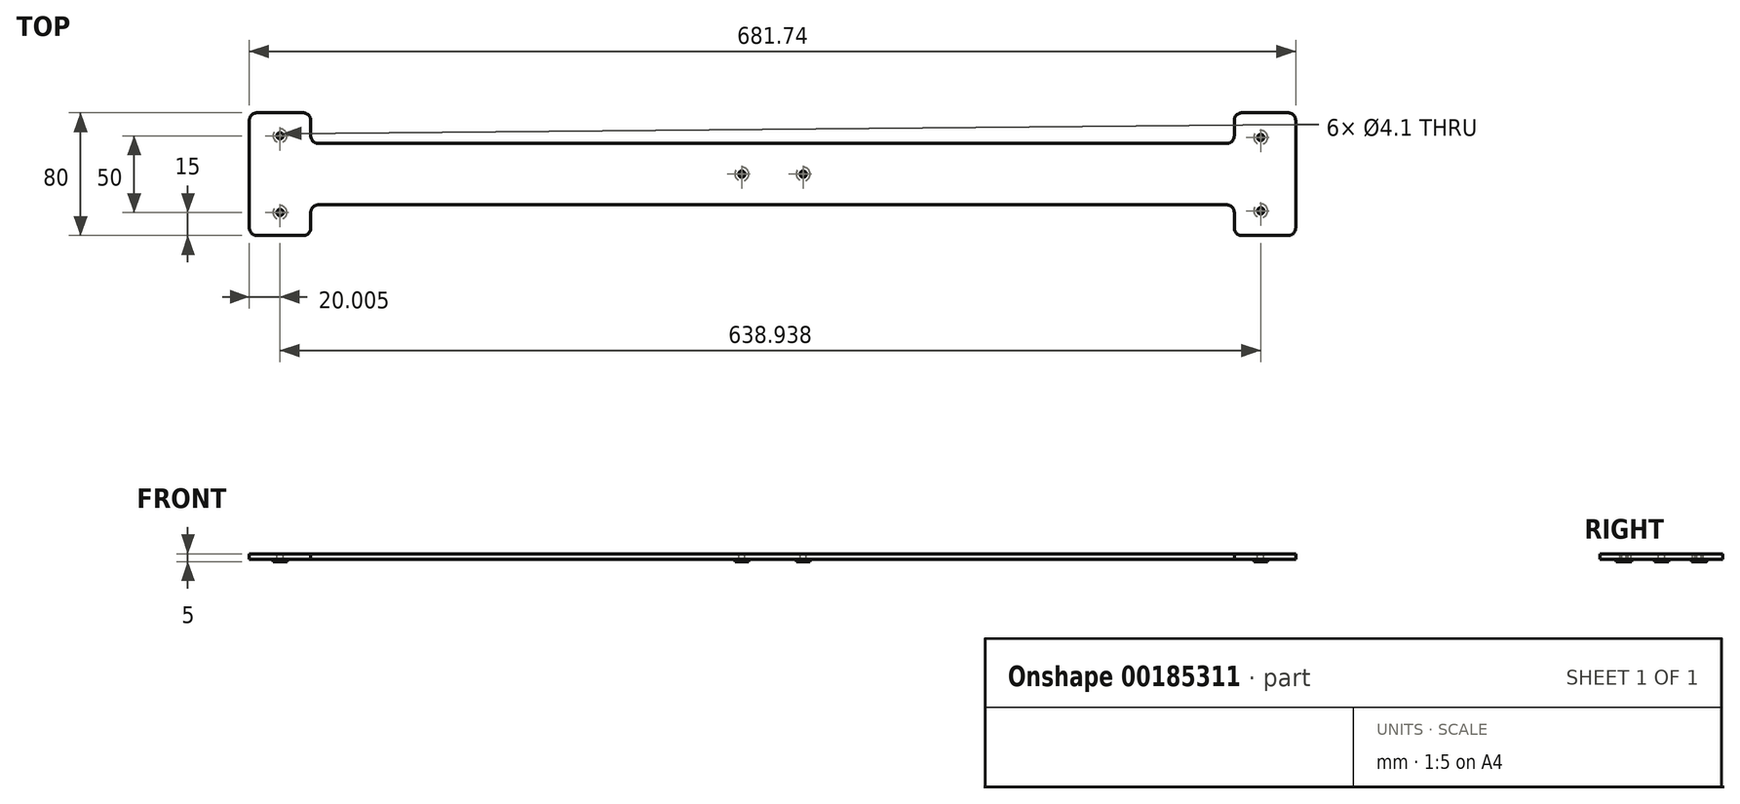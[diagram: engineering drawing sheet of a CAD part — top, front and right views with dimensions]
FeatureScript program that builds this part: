
annotation { "Feature Type Name" : "Feature", "Feature Type Description" : "" }
export const myFeature = defineFeature(function(context is Context, id is Id, definition is map)
    precondition{}
    {
        {
            var Q0;
            Q0=qCreatedBy(makeId("Top.planeOp"),FACE);
            var sketch = newSketch(context, id + "F0", { "sketchPlane" : qUnion([Q0])});
            skLineSegment(sketch, "E0.bottom", {"start": v(340.87, 40) * mm, "end": v(-340.87, 40) * mm, "construction": true});
            skLineSegment(sketch, "E0.top", {"start": v(340.87, -40) * mm, "end": v(-340.87, -40) * mm, "construction": true});
            skLineSegment(sketch, "E0.left", {"start": v(340.87, 40) * mm, "end": v(340.87, -40) * mm});
            skLineSegment(sketch, "E0.right", {"start": v(-340.87, 40) * mm, "end": v(-340.87, -40) * mm});
            skPoint(sketch, "E0.middle", {"position": v(0, 0) * mm});
            skLineSegment(sketch, "E1", {"start": v(-340.87, 40) * mm, "end": v(-300.87, 40) * mm});
            skLineSegment(sketch, "E2", {"start": v(-300.87, 40) * mm, "end": v(-300.87, 20) * mm});
            skLineSegment(sketch, "E3", {"start": v(-300.87, 20) * mm, "end": v(300.87, 20) * mm});
            skLineSegment(sketch, "E4", {"start": v(300.87, 20) * mm, "end": v(300.87, 40) * mm});
            skLineSegment(sketch, "E5", {"start": v(300.87, 40) * mm, "end": v(340.87, 40) * mm});
            skLineSegment(sketch, "E6", {"start": v(340.87, -40) * mm, "end": v(300.87, -40) * mm});
            skLineSegment(sketch, "E7", {"start": v(300.87, -40) * mm, "end": v(300.87, -20) * mm});
            skLineSegment(sketch, "E8", {"start": v(300.87, -20) * mm, "end": v(-300.87, -20) * mm});
            skLineSegment(sketch, "E9", {"start": v(-300.87, -20) * mm, "end": v(-300.87, -40) * mm});
            skLineSegment(sketch, "E10", {"start": v(-300.87, -40) * mm, "end": v(-340.87, -40) * mm});
            skSolve(sketch);
        }
        {
            var Q0;
            Q0 = qSketchRegion(id + "F0", true);
            extrude(context, id + "F1", {"entities" : qUnion([Q0]), "depth" : 3.42 * mm});
        }
        {
            var Q0;
            Q0=makeQuery(id+"F1.opExtrude","SWEPT_EDGE",EDGE,{"disambiguationData":[OSD([sQuery(id+"F0.wireOp",EDGE,"E0.right"),sQuery(id+"F0.wireOp",EDGE,"E1")])]});
            var Q1;
            Q1=makeQuery(id+"F1.opExtrude","SWEPT_EDGE",EDGE,{"disambiguationData":[OSD([sQuery(id+"F0.wireOp",EDGE,"E0.right"),sQuery(id+"F0.wireOp",EDGE,"E10")])]});
            var Q2;
            Q2=makeQuery(id+"F1.opExtrude","SWEPT_EDGE",EDGE,{"disambiguationData":[OSD([sQuery(id+"F0.wireOp",EDGE,"E1"),sQuery(id+"F0.wireOp",EDGE,"E2")])]});
            var Q3;
            Q3=makeQuery(id+"F1.opExtrude","SWEPT_EDGE",EDGE,{"disambiguationData":[OSD([sQuery(id+"F0.wireOp",EDGE,"E2"),sQuery(id+"F0.wireOp",EDGE,"E3")])]});
            var Q4;
            Q4=makeQuery(id+"F1.opExtrude","SWEPT_EDGE",EDGE,{"disambiguationData":[OSD([sQuery(id+"F0.wireOp",EDGE,"E8"),sQuery(id+"F0.wireOp",EDGE,"E9")])]});
            var Q5;
            Q5=makeQuery(id+"F1.opExtrude","SWEPT_EDGE",EDGE,{"disambiguationData":[OSD([sQuery(id+"F0.wireOp",EDGE,"E9"),sQuery(id+"F0.wireOp",EDGE,"E10")])]});
            var Q6;
            Q6=makeQuery(id+"F1.opExtrude","SWEPT_EDGE",EDGE,{"disambiguationData":[OSD([sQuery(id+"F0.wireOp",EDGE,"E3"),sQuery(id+"F0.wireOp",EDGE,"E4")])]});
            var Q7;
            Q7=makeQuery(id+"F1.opExtrude","SWEPT_EDGE",EDGE,{"disambiguationData":[OSD([sQuery(id+"F0.wireOp",EDGE,"E4"),sQuery(id+"F0.wireOp",EDGE,"E5")])]});
            var Q8;
            Q8=makeQuery(id+"F1.opExtrude","SWEPT_EDGE",EDGE,{"disambiguationData":[OSD([sQuery(id+"F0.wireOp",EDGE,"E0.left"),sQuery(id+"F0.wireOp",EDGE,"E5")])]});
            var Q9;
            Q9=makeQuery(id+"F1.opExtrude","SWEPT_EDGE",EDGE,{"disambiguationData":[OSD([sQuery(id+"F0.wireOp",EDGE,"E6"),sQuery(id+"F0.wireOp",EDGE,"E7")])]});
            var Q10;
            Q10=makeQuery(id+"F1.opExtrude","SWEPT_EDGE",EDGE,{"disambiguationData":[OSD([sQuery(id+"F0.wireOp",EDGE,"E7"),sQuery(id+"F0.wireOp",EDGE,"E8")])]});
            var Q11;
            Q11=makeQuery(id+"F1.opExtrude","SWEPT_EDGE",EDGE,{"disambiguationData":[OSD([sQuery(id+"F0.wireOp",EDGE,"E0.left"),sQuery(id+"F0.wireOp",EDGE,"E6")])]});
            fillet(context, id + "F2", {"entities" : qUnion([Q0, Q1, Q2, Q3, Q4, Q5, Q6, Q7, Q8, Q9, Q10, Q11]), "radius" : 5 * mm, "tangentPropagation" : true, "allowEdgeOverflow" : false});
        }
        {
            var Q0;
            Q0=makeQuery(id+"F1.opExtrude","CAP_FACE",FACE,{"disambiguationData":[OSD([sQuery(id+"F0.wireOp",EDGE,"E0.left"),sQuery(id+"F0.wireOp",EDGE,"E0.right"),sQuery(id+"F0.wireOp",EDGE,"E1"),sQuery(id+"F0.wireOp",EDGE,"E2"),sQuery(id+"F0.wireOp",EDGE,"E3"),sQuery(id+"F0.wireOp",EDGE,"E4"),sQuery(id+"F0.wireOp",EDGE,"E5"),sQuery(id+"F0.wireOp",EDGE,"E6"),sQuery(id+"F0.wireOp",EDGE,"E7"),sQuery(id+"F0.wireOp",EDGE,"E8"),sQuery(id+"F0.wireOp",EDGE,"E9"),sQuery(id+"F0.wireOp",EDGE,"E10")])],"isStart":false});
            var sketch = newSketch(context, id + "F3", { "sketchPlane" : qUnion([Q0])});
            skLineSegment(sketch, "E11", {"start": v(-320.87, 25) * mm, "end": v(-320.87, -25) * mm, "construction": true});
            skLineSegment(sketch, "E12", {"start": v(-320.87, 0) * mm, "end": v(-20, 0) * mm, "construction": true});
            skLineSegment(sketch, "E13", {"start": v(-20, 0) * mm, "end": v(20, 0) * mm, "construction": true});
            skLineSegment(sketch, "E14", {"start": v(20, 0) * mm, "end": v(318.07, 0) * mm, "construction": true});
            skLineSegment(sketch, "E15", {"start": v(318.07, 23.9) * mm, "end": v(318.07, -23.9) * mm, "construction": true});
            skCircle(sketch, "E16", {"center": v(-320.87, 25) * mm, "radius": 4.5 * mm});
            skCircle(sketch, "E17", {"center": v(-320.87, -25) * mm, "radius": 4.5 * mm});
            skCircle(sketch, "E18", {"center": v(-20, 0) * mm, "radius": 4.5 * mm});
            skCircle(sketch, "E19", {"center": v(20, 0) * mm, "radius": 4.5 * mm});
            skCircle(sketch, "E20", {"center": v(318.07, 23.9) * mm, "radius": 4.5 * mm});
            skCircle(sketch, "E21", {"center": v(318.07, -23.9) * mm, "radius": 4.5 * mm});
            skSolve(sketch);
        }
        {
            var Q0;
            Q0 = qSketchRegion(id + "F3", true);
            extrude(context, id + "F4", {"entities" : qUnion([Q0]), "operationType" : NewBodyOperationType.ADD, "oppositeDirection" : true, "depth" : 5 * mm});
        }
        {
            var Q0;
            Q0=sQuery(id+"F3.wireOp",VERTEX,"E17.center");
            var Q1;
            Q1=sQuery(id+"F3.wireOp",VERTEX,"E18.center");
            var Q2;
            Q2=sQuery(id+"F3.wireOp",VERTEX,"E19.center");
            var Q3;
            Q3=sQuery(id+"F3.wireOp",VERTEX,"E20.center");
            var Q4;
            Q4=sQuery(id+"F3.wireOp",VERTEX,"E21.center");
            var Q5;
            Q5=sQuery(id+"F3.wireOp",VERTEX,"E16.center");
            var Q6;
            Q6=makeQuery(id+"F1.opExtrude","SWEPT_BODY",BODY,{"disambiguationData":[OSD([sQuery(id+"F0.wireOp",EDGE,"E0.left"),sQuery(id+"F0.wireOp",EDGE,"E0.right"),sQuery(id+"F0.wireOp",EDGE,"E1"),sQuery(id+"F0.wireOp",EDGE,"E2"),sQuery(id+"F0.wireOp",EDGE,"E3"),sQuery(id+"F0.wireOp",EDGE,"E4"),sQuery(id+"F0.wireOp",EDGE,"E5"),sQuery(id+"F0.wireOp",EDGE,"E6"),sQuery(id+"F0.wireOp",EDGE,"E7"),sQuery(id+"F0.wireOp",EDGE,"E8"),sQuery(id+"F0.wireOp",EDGE,"E9"),sQuery(id+"F0.wireOp",EDGE,"E10")])]});
            hole(context, id + "F5", {"style" : HoleStyle.SIMPLE, "endStyle" : HoleEndStyle.THROUGH, "standardTappedOrClearance" : lookupTablePath({ "standard" : "ISO", "engagement" : "75%", "pitch" : "0.9 mm", "size" : "M5", "type" : "Tapped" }), "standardBlindInLast" : lookupTablePath({ "standard" : "ISO", "engagement" : "75%", "pitch" : "0.9 mm", "size" : "M5", "type" : "Tapped" }), "holeDiameter" : 4.1 * mm, "locations" : qUnion([Q0, Q1, Q2, Q3, Q4, Q5]), "scope" : qUnion([Q6]), "isTappedThrough" : true, "showTappedDepth" : true});
        }
    });
